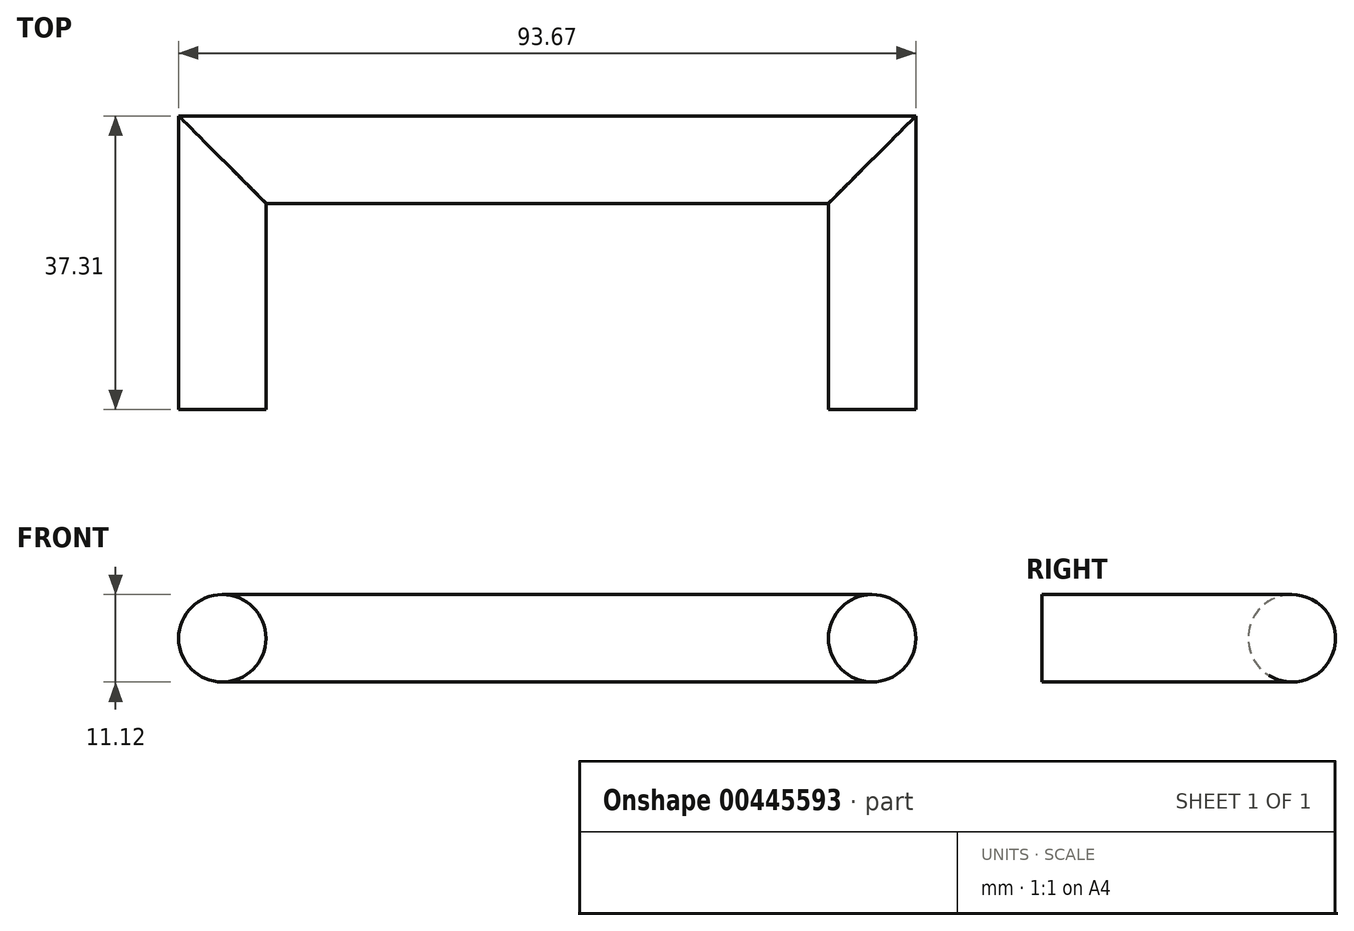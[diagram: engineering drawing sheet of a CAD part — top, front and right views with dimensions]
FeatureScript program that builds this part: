
annotation { "Feature Type Name" : "Feature", "Feature Type Description" : "" }
export const myFeature = defineFeature(function(context is Context, id is Id, definition is map)
    precondition{}
    {
        {
            var Q0;
            Q0=qCreatedBy(makeId("Front.planeOp"),FACE);
            var sketch = newSketch(context, id + "F0", { "sketchPlane" : qUnion([Q0])});
            skCircle(sketch, "E0", {"center": v(0, 0) * mm, "radius": 5.56 * mm});
            skSolve(sketch);
        }
        {
            var Q0;
            Q0=qCreatedBy(makeId("Top.planeOp"),FACE);
            var sketch = newSketch(context, id + "F1", { "sketchPlane" : qUnion([Q0])});
            skLineSegment(sketch, "E1", {"start": v(0, 31.75) * mm, "end": v(0, 0) * mm});
            skLineSegment(sketch, "E2", {"start": v(0, 31.75) * mm, "end": v(-82.55, 31.75) * mm});
            skLineSegment(sketch, "E3", {"start": v(-82.55, 0) * mm, "end": v(-82.55, 31.75) * mm});
            skSolve(sketch);
        }
        {
            var Q0;
            Q0=makeQuery(id+"F0.imprint","IMPRINT",FACE,{"disambiguationData":[TD([[makeQuery(id+"F0.imprint","IMPRINT",EDGE,{"derivedFrom":sQuery(id+"F0.wireOp",EDGE,"E0")}),1.0]])]});
            var Q1;
            Q1=sQuery(id+"F1.wireOp",EDGE,"E2");
            var Q2;
            Q2=sQuery(id+"F1.wireOp",EDGE,"E3");
            var Q3;
            Q3=sQuery(id+"F1.wireOp",EDGE,"E1");
            sweep(context, id + "F2", {"profiles" : qUnion([Q0]), "path" : qUnion([Q1, Q2, Q3])});
        }
    });
